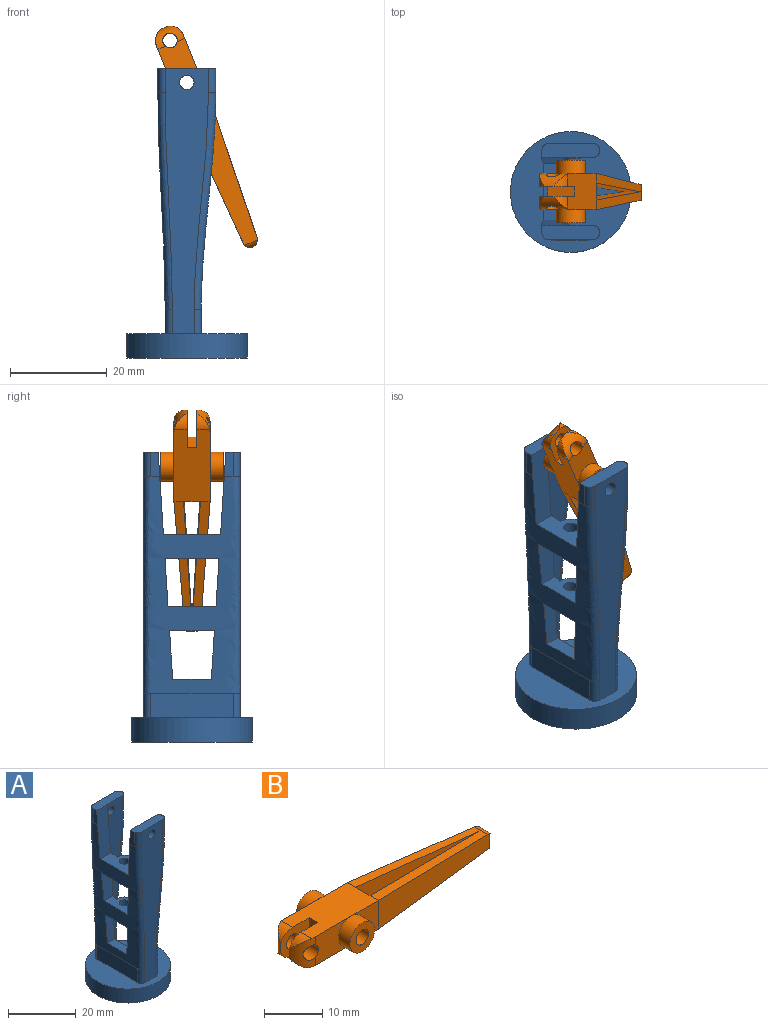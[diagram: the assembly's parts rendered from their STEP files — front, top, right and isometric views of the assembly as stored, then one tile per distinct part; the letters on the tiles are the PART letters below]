
ASSEMBLY  parts=2 mates=1
PART A: 51 faces, bbox 25.9x25.9x60.9 mm
  f0: bspline ~45x11mm, area 61.4mm2, adj f6,f7,f10,f26,f36,f37,f38,f39
  f1: plane 5x0.32mm, normal (1,0,0), area 0.8mm2, adj f7,f20,f45
  f2: plane 5x0.32mm, normal (1,0,0), area 0.8mm2, adj f6,f19,f44
  f3: plane 5x1.82mm, normal (-1,0,0), area 8.3mm2, adj f8,f32,f33,f44
  f4: plane 5x1.82mm, normal (-1,0,0), area 8.3mm2, adj f5,f8,f29,f45
  f5: plane 12x3mm, normal (0,0,1), area 34.6mm2, adj f4,f20,f22,f29,f30,f45
  f6: bspline ~45x5.5mm, area 94.6mm2, adj f0,f2,f9,f19,f27,f40,f41,f43
  f7: bspline ~45x5.5mm, area 94.6mm2, adj f0,f1,f9,f20,f28,f40,f41,f42
  f8: bspline ~45x20mm, area 634.3mm2, adj f3,f4,f17,f22,f23,f24,f25,f29
  f9: cylinder r=3mm len=6mm, axis (0,0,1), area 47.1mm2, adj f6,f7,f40,f46
  f10: cylinder r=3mm len=6mm, axis (0,0,1), area 49.1mm2, adj f0,f36,f41
  f11: cylinder r=12.5mm len=25mm, axis (0,0,-1), area 392.7mm2, adj f12,f13
  f12: plane 25x25mm, normal (0,0,1), area 383.1mm2, adj f11,f15,f17,f18,f19,f20,f21,f22
  f13: plane 25x25mm, normal (0,0,-1), area 483.8mm2, adj f11,f14
  f14: cylinder r=1.5mm len=6.75mm, axis (0,0,-1), area 63.6mm2, adj f13,f16
  f15: cylinder r=3mm len=6mm, axis (0,0,-1), area 22mm2, adj f12,f16,f26
  f16: plane 6x4.5mm, normal (0,0,1), area 15.7mm2, adj f14,f15,f26
  f17: plane 55.87x9.87mm, normal (0,1,0), area 365mm2, adj f8,f12,f18,f25,f31,f32,f33,f35
  f18: cylinder r=1.5mm len=5mm, axis (0,0,-1), area 23.6mm2, adj f12,f17,f19,f35
  f19: plane 55.37x6.37mm, normal (0,-1,0), area 200.8mm2, adj f2,f6,f12,f18,f27,f31,f33,f35
  f20: plane 55.37x6.37mm, normal (0,1,0), area 200.8mm2, adj f1,f5,f7,f12,f21,f28,f30,f34
  f21: cylinder r=1.5mm len=5mm, axis (0,0,-1), area 23.6mm2, adj f12,f20,f22,f34
  f22: plane 55.87x9.87mm, normal (0,-1,0), area 365mm2, adj f5,f8,f12,f21,f23,f29,f30,f34
  f23: cylinder r=1.5mm len=5mm, axis (0,0,-1), area 11.8mm2, adj f8,f12,f22,f24
  f24: plane 17x5mm, normal (-1,0,0), area 85mm2, adj f8,f12,f23,f25
  f25: cylinder r=1.5mm len=5mm, axis (0,0,-1), area 11.8mm2, adj f8,f12,f17,f24
  f26: plane 11x5mm, normal (1,0,0), area 45.9mm2, adj f0,f12,f15,f16,f27,f28
  f27: cylinder r=1.5mm len=5mm, axis (0,0,-1), area 11.8mm2, adj f6,f12,f19,f26
  f28: cylinder r=1.5mm len=5mm, axis (0,0,-1), area 11.8mm2, adj f7,f12,f20,f26
  f29: cylinder r=1.5mm len=5mm, axis (0,0,1), area 11.8mm2, adj f4,f5,f8,f22
  f30: cylinder r=1.5mm len=5mm, axis (0,0,1), area 23.6mm2, adj f5,f20,f22,f34
  f31: cylinder r=1.5mm len=5mm, axis (0,0,1), area 23.6mm2, adj f17,f19,f33,f35
  f32: cylinder r=1.5mm len=5mm, axis (0,0,1), area 11.8mm2, adj f3,f8,f17,f33
  f33: plane 12x3mm, normal (0,0,1), area 34.6mm2, adj f3,f17,f19,f31,f32,f44
  f34: bspline ~45x7.63mm, area 212.1mm2, adj f20,f21,f22,f30
  f35: bspline ~45x7.63mm, area 212.1mm2, adj f17,f18,f19,f31
  f36: plane 9.3x6.33mm, normal (0,0,-1), area 37.4mm2, adj f0,f8,f10,f37,f38,f47
  f37: plane 10.28x3.58mm, normal (0,1,0.06), area 31.2mm2, adj f0,f8,f36,f39
  f38: plane 10.28x3.58mm, normal (0,-1,0.06), area 31.2mm2, adj f0,f8,f36,f39
  f39: plane 8x3.01mm, normal (0,0,1), area 24mm2, adj f0,f8,f37,f38
  f40: plane 11.24x7.07mm, normal (0,0,-1), area 52.5mm2, adj f6,f7,f8,f9,f42,f43,f48
  f41: plane 9.94x6.55mm, normal (0,0,1), area 41.8mm2, adj f0,f6,f7,f8,f10,f42,f43,f47
  f42: plane 10.2x4.45mm, normal (0,1,0.06), area 39.6mm2, adj f7,f8,f40,f41
  f43: plane 10.2x4.45mm, normal (0,-1,0.06), area 39.6mm2, adj f6,f8,f40,f41
  f44: plane 17.14x4.8mm, normal (0,-1,0.06), area 76.3mm2, adj f2,f3,f6,f8,f33,f46
  f45: plane 17.14x4.8mm, normal (0,1,0.06), area 76.3mm2, adj f1,f4,f5,f7,f8,f46
  f46: plane 11.87x7.27mm, normal (0,0,1), area 57.6mm2, adj f6,f7,f8,f9,f44,f45,f48
  f47: cylinder r=1.5mm len=5mm, axis (0,0,1), area 47.1mm2, adj f36,f41
  f48: cylinder r=1.5mm len=5mm, axis (0,0,1), area 47.1mm2, adj f40,f46
  f49: cylinder r=1.5mm len=3mm, axis (0,1,0), area 28.3mm2, adj f20,f22
  f50: cylinder r=1.5mm len=3mm, axis (0,1,0), area 28.3mm2, adj f17,f19
PART B: 33 faces, bbox 48.9x13x6 mm
  f0: plane 28x6mm, normal (-0.06,1,0), area 129.1mm2, adj f1,f24,f26,f27
  f1: plane 28x6mm, normal (-0.06,-1,0), area 129.1mm2, adj f0,f24,f26,f27
  f2: plane 16x7.5mm, normal (0,0,1), area 112mm2, adj f4,f5,f7,f10,f11,f12,f20,f21
  f3: cylinder r=2mm len=2.88mm, axis (0,0,1), area 3.3mm2, adj f18,f25,f28
  f4: plane 6.86x6mm, normal (0,1,0), area 30.9mm2, adj f2,f6,f8,f20,f21,f31,f32
  f5: plane 6.86x6mm, normal (0,-1,0), area 30.9mm2, adj f2,f6,f9,f20,f22,f29,f30
  f6: plane 16x7.5mm, normal (0,0,-1), area 112mm2, adj f4,f5,f7,f10,f11,f12,f20,f21
  f7: plane 6.63x6mm, normal (0,1,0), area 25.7mm2, adj f2,f6,f14,f23
  f8: cylinder r=1.5mm len=3mm, axis (0,1,0), area 23.8mm2, adj f4,f11,f21
  f9: cylinder r=1.5mm len=3mm, axis (0,1,0), area 23.8mm2, adj f5,f12,f22
  f10: plane 6.63x6mm, normal (0,-1,0), area 25.7mm2, adj f2,f6,f16,f18
  f11: plane 8.62x6mm, normal (0,-1,0), area 36.2mm2, adj f2,f6,f8,f16,f21
  f12: plane 8.62x6mm, normal (0,1,0), area 36.2mm2, adj f2,f6,f9,f14,f22
  f13: plane 6x6mm, normal (0,1,0), area 21.2mm2, adj f14,f15
  f14: cylinder r=3mm len=6mm, axis (0,1,0), area 51.8mm2, adj f7,f12,f13
  f15: cylinder r=1.5mm len=13mm, axis (0,1,0), area 122.5mm2, adj f13,f17
  f16: cylinder r=3mm len=6mm, axis (0,1,0), area 51.8mm2, adj f10,f11,f17
  f17: plane 6x6mm, normal (0,-1,0), area 21.2mm2, adj f15,f16
  f18: plane 29.07x6mm, normal (0.07,-1,0), area 132.4mm2, adj f3,f10,f25,f26,f27,f28
  f19: cylinder r=2mm len=2.46mm, axis (0,0,1), area 1.9mm2, adj f23,f25,f28
  f20: plane 6x2mm, normal (-1,0,0), area 12mm2, adj f2,f4,f5,f6
  f21: cylinder r=3.75mm len=6mm, axis (0,0,1), area 17mm2, adj f2,f4,f6,f8,f11,f31,f32
  f22: cylinder r=3.75mm len=6mm, axis (0,0,1), area 17mm2, adj f2,f5,f6,f9,f12,f29,f30
  f23: plane 29.41x6mm, normal (0.08,1,0), area 133.5mm2, adj f7,f19,f25,f26,f27,f28
  f24: plane 6x3.5mm, normal (1,0,0), area 21mm2, adj f0,f1,f2,f6
  f25: cylinder r=1.58mm len=3.22mm, axis (0,1,0), area 5.1mm2, adj f3,f18,f19,f23,f26
  f26: plane 28.5x7.5mm, normal (0.05,0,-1), area 104mm2, adj f0,f1,f6,f18,f23,f25
  f27: plane 28.5x7.5mm, normal (0.05,0,1), area 104mm2, adj f0,f1,f2,f18,f23,f28
  f28: cylinder r=1.58mm len=3.22mm, axis (0,1,0), area 5.1mm2, adj f3,f18,f19,f23,f27
  f29: cylinder r=3mm len=2.86mm, axis (0,1,0), area 6.2mm2, adj f2,f5,f22
  f30: cylinder r=3mm len=2.86mm, axis (0,1,0), area 6.2mm2, adj f5,f6,f22
  f31: cylinder r=3mm len=2.86mm, axis (0,1,0), area 6.2mm2, adj f2,f4,f21
  f32: cylinder r=3mm len=2.86mm, axis (0,1,0), area 6.2mm2, adj f4,f6,f21
PLACE A at identity fixed
PLACE B rot(axis=(0,1,0),68.2deg) t=(-52.91,0,35.79)mm
MATE revolute B.f15 <-> A.f49  axis (0,1,0) through (0,-6.5,57)mm
